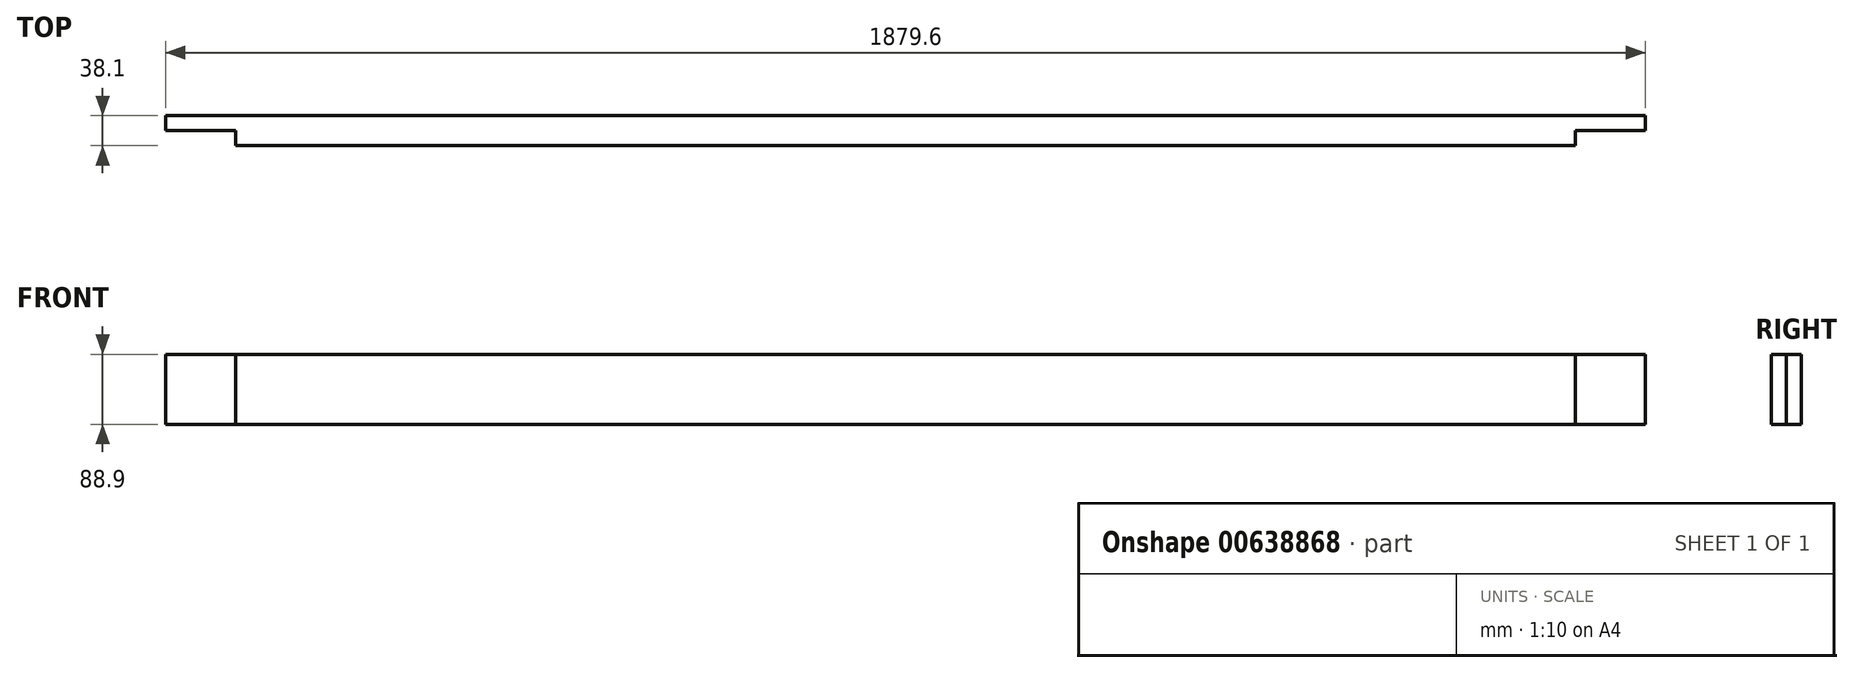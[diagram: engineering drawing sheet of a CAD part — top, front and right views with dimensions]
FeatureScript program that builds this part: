
annotation { "Feature Type Name" : "Feature", "Feature Type Description" : "" }
export const myFeature = defineFeature(function(context is Context, id is Id, definition is map)
    precondition{}
    {
        {
            var Q0;
            Q0=qCreatedBy(makeId("Right.planeOp"),FACE);
            var sketch = newSketch(context, id + "F0", { "sketchPlane" : qUnion([Q0])});
            skLineSegment(sketch, "E0.bottom", {"start": v(19.05, 44.45) * mm, "end": v(-19.05, 44.45) * mm});
            skLineSegment(sketch, "E0.top", {"start": v(19.05, -44.45) * mm, "end": v(-19.05, -44.45) * mm});
            skLineSegment(sketch, "E0.left", {"start": v(19.05, 44.45) * mm, "end": v(19.05, -44.45) * mm});
            skLineSegment(sketch, "E0.right", {"start": v(-19.05, 44.45) * mm, "end": v(-19.05, -44.45) * mm});
            skPoint(sketch, "E0.middle", {"position": v(0, 0) * mm});
            skSolve(sketch);
        }
        {
            var Q0;
            Q0 = qSketchRegion(id + "F0", true);
            extrude(context, id + "F1", {"entities" : qUnion([Q0]), "depth" : 939.8 * mm, "offsetDistance" : 25.4 * mm});
        }
        {
            var Q0;
            {var subQ0=makeQuery(id+"F1.opExtrude","SWEPT_FACE",FACE,{"disambiguationData":[OSD([sQuery(id+"F0.wireOp",EDGE,"E0.bottom")])]});Q0=makeQuery(id+"F4.boolean.opBoolean","MERGE",FACE,{"derivedFrom":[subQ0,makeQuery(id+"F4.opPattern","COPY",FACE,{"derivedFrom":subQ0,"instanceName":"1"})]});}
            var sketch = newSketch(context, id + "F2", { "sketchPlane" : qUnion([Q0])});
            skLineSegment(sketch, "E1.bottom", {"start": v(939.8, -19.05) * mm, "end": v(850.9, -19.05) * mm});
            skLineSegment(sketch, "E1.top", {"start": v(939.8, 0) * mm, "end": v(850.9, 0) * mm});
            skLineSegment(sketch, "E1.left", {"start": v(939.8, -19.05) * mm, "end": v(939.8, 0) * mm});
            skLineSegment(sketch, "E1.right", {"start": v(850.9, -19.05) * mm, "end": v(850.9, 0) * mm});
            skSolve(sketch);
        }
        {
            var Q0;
            Q0 = qSketchRegion(id + "F2", true);
            extrude(context, id + "F3", {"entities" : qUnion([Q0]), "operationType" : NewBodyOperationType.REMOVE, "endBound" : BoundingType.UP_TO_NEXT, "oppositeDirection" : true, "depth" : 25.4 * mm, "offsetDistance" : 25.4 * mm});
        }
        {
            var Q0;
            Q0=makeQuery(id+"F1.opExtrude","SWEPT_BODY",BODY,{"disambiguationData":[OSD([sQuery(id+"F0.wireOp",EDGE,"E0.bottom"),sQuery(id+"F0.wireOp",EDGE,"E0.top"),sQuery(id+"F0.wireOp",EDGE,"E0.left"),sQuery(id+"F0.wireOp",EDGE,"E0.right")])]});
            var Q1;
            Q1=qCreatedBy(makeId("Right.planeOp"),FACE);
            mirror(context, id + "F4", {"operationType" : NewBodyOperationType.ADD, "entities" : qUnion([Q0]), "mirrorPlane" : qUnion([Q1])});
        }
    });
